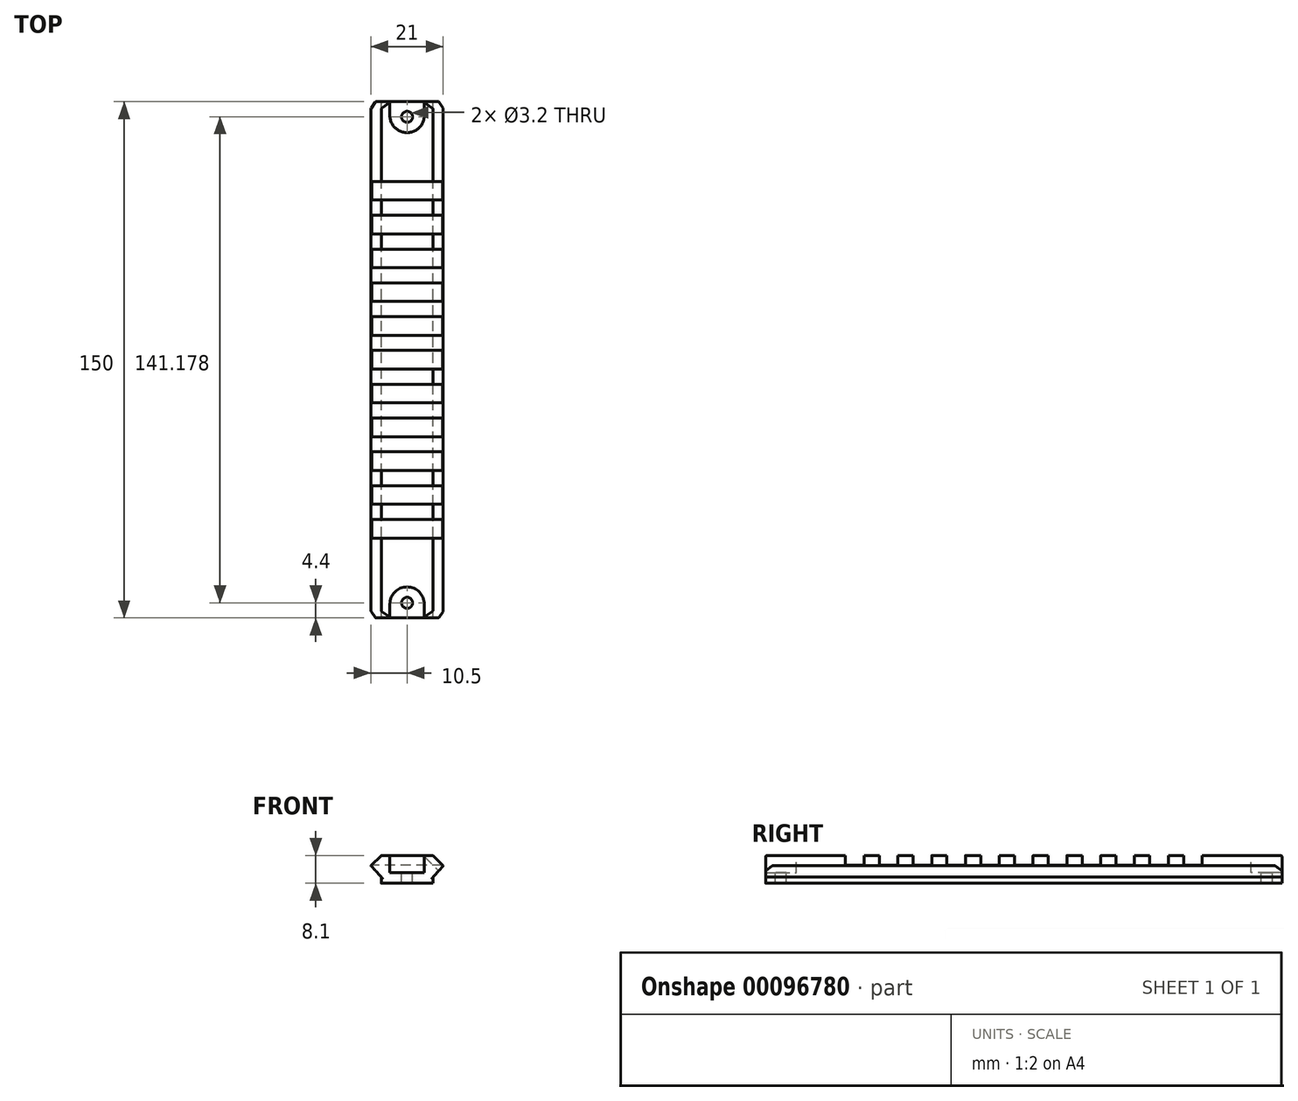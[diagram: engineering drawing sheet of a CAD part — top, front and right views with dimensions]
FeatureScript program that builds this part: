
annotation { "Feature Type Name" : "Feature", "Feature Type Description" : "" }
export const myFeature = defineFeature(function(context is Context, id is Id, definition is map)
    precondition{}
    {
        {
            var Q0;
            Q0=qCreatedBy(makeId("Front.planeOp"),FACE);
            var sketch = newSketch(context, id + "F0", { "sketchPlane" : qUnion([Q0])});
            skPoint(sketch, "E0", {"position": v(7.5, 0) * mm});
            skPoint(sketch, "E1", {"position": v(-7.5, 0) * mm});
            skPoint(sketch, "E2", {"position": v(0, 3.3) * mm});
            skPoint(sketch, "E3", {"position": v(0, -4.8) * mm});
            skLineSegment(sketch, "E4", {"start": v(7.5, -4.8) * mm, "end": v(-7.5, -4.8) * mm});
            skLineSegment(sketch, "E5", {"start": v(7.5, -4.8) * mm, "end": v(7.5, -3) * mm});
            skLineSegment(sketch, "E6", {"start": v(-7.5, -3) * mm, "end": v(-7.5, -4.8) * mm});
            skLineSegment(sketch, "E7", {"start": v(-7.5, -3) * mm, "end": v(-10.5, 0.3) * mm});
            skLineSegment(sketch, "E8", {"start": v(7.5, -3) * mm, "end": v(10.5, 0.3) * mm});
            skPoint(sketch, "E9", {"position": v(7.5, 3.3) * mm});
            skPoint(sketch, "E10", {"position": v(-7.5, 3.3) * mm});
            skLineSegment(sketch, "E11", {"start": v(-10.5, 0.3) * mm, "end": v(-7.5, 3.3) * mm});
            skLineSegment(sketch, "E12", {"start": v(10.5, 0.3) * mm, "end": v(7.5, 3.3) * mm});
            skLineSegment(sketch, "E13", {"start": v(-7.5, 3.3) * mm, "end": v(7.5, 3.3) * mm});
            skSolve(sketch);
        }
        {
            var Q0;
            Q0=qSketchRegion(id+"F0",true);
            extrude(context, id + "F1", {"entities" : qUnion([Q0]), "endBound" : BoundingType.SYMMETRIC, "depth" : 150 * mm});
        }
        {
            var Q0;
            Q0=makeQuery(id+"F1.opExtrude","SWEPT_FACE",FACE,{"disambiguationData":[OSD([sQuery(id+"F0.wireOp",EDGE,"E13")])]});
            var sketch = newSketch(context, id + "F2", { "sketchPlane" : qUnion([Q0])});
            skPoint(sketch, "E14", {"position": v(0, 2.7) * mm});
            skPoint(sketch, "E15", {"position": v(0, -2.7) * mm});
            skLineSegment(sketch, "E16", {"start": v(-14, -2.7) * mm, "end": v(14, -2.7) * mm});
            skLineSegment(sketch, "E17", {"start": v(14, -2.7) * mm, "end": v(14, 2.7) * mm});
            skLineSegment(sketch, "E18", {"start": v(14, 2.7) * mm, "end": v(-14, 2.7) * mm});
            skLineSegment(sketch, "E19", {"start": v(-14, -2.7) * mm, "end": v(-14, 2.7) * mm});
            skLineSegment(sketch, "E20", {"start": v(0, 75) * mm, "end": v(0, 60) * mm});
            skPoint(sketch, "E20.endSnap0", {"position": v(0, 75) * mm});
            skLineSegment(sketch, "E21.0.1.0", {"start": v(-14, 7.12) * mm, "end": v(-14, 12.52) * mm});
            skLineSegment(sketch, "E21.0.1.1", {"start": v(14.12, 12.52) * mm, "end": v(-14, 12.52) * mm});
            skLineSegment(sketch, "E21.0.1.2", {"start": v(-14, 7.12) * mm, "end": v(14.12, 7.12) * mm});
            skLineSegment(sketch, "E21.0.1.3", {"start": v(14.12, 7.12) * mm, "end": v(14.12, 12.52) * mm});
            skLineSegment(sketch, "E21.0.2.0", {"start": v(-14, 16.94) * mm, "end": v(-14, 22.34) * mm});
            skLineSegment(sketch, "E21.0.2.1", {"start": v(14.33, 22.34) * mm, "end": v(-14, 22.34) * mm});
            skLineSegment(sketch, "E21.0.2.2", {"start": v(-14, 16.94) * mm, "end": v(14.33, 16.94) * mm});
            skLineSegment(sketch, "E21.0.2.3", {"start": v(14.33, 16.94) * mm, "end": v(14.33, 22.34) * mm});
            skLineSegment(sketch, "E21.0.3.0", {"start": v(-14, 26.76) * mm, "end": v(-14, 32.16) * mm});
            skLineSegment(sketch, "E21.0.3.1", {"start": v(14.82, 32.16) * mm, "end": v(-14, 32.16) * mm});
            skLineSegment(sketch, "E21.0.3.2", {"start": v(-14, 26.76) * mm, "end": v(14.82, 26.76) * mm});
            skLineSegment(sketch, "E21.0.3.3", {"start": v(14.82, 26.76) * mm, "end": v(14.82, 32.16) * mm});
            skLineSegment(sketch, "E21.direction2", {"start": v(-14, -2.7) * mm, "end": v(-14, 7.12) * mm, "construction": true});
            skLineSegment(sketch, "E22.0.1.0", {"start": v(-14, -12.52) * mm, "end": v(14.53, -12.52) * mm});
            skLineSegment(sketch, "E22.0.1.1", {"start": v(-14, -12.52) * mm, "end": v(-14, -7.1) * mm});
            skLineSegment(sketch, "E22.0.1.2", {"start": v(14.53, -7.1) * mm, "end": v(-14, -7.1) * mm});
            skLineSegment(sketch, "E22.0.1.3", {"start": v(14.53, -12.52) * mm, "end": v(14.53, -7.1) * mm});
            skLineSegment(sketch, "E22.0.2.0", {"start": v(-14, -22.33) * mm, "end": v(15.6, -22.33) * mm});
            skLineSegment(sketch, "E22.0.2.1", {"start": v(-14, -22.33) * mm, "end": v(-14, -16.93) * mm});
            skLineSegment(sketch, "E22.0.2.2", {"start": v(15.6, -16.93) * mm, "end": v(-14, -16.93) * mm});
            skLineSegment(sketch, "E22.0.2.3", {"start": v(15.6, -22.33) * mm, "end": v(15.6, -16.93) * mm});
            skLineSegment(sketch, "E22.0.3.0", {"start": v(-14, -32.15) * mm, "end": v(15.9, -32.15) * mm});
            skLineSegment(sketch, "E22.0.3.1", {"start": v(-14, -32.15) * mm, "end": v(-14, -26.75) * mm});
            skLineSegment(sketch, "E22.0.3.2", {"start": v(15.9, -26.75) * mm, "end": v(-14, -26.75) * mm});
            skLineSegment(sketch, "E22.0.3.3", {"start": v(15.9, -32.15) * mm, "end": v(15.9, -26.75) * mm});
            skLineSegment(sketch, "E22.direction2", {"start": v(-14, -2.7) * mm, "end": v(-14, -12.52) * mm, "construction": true});
            skLineSegment(sketch, "E23.1.0.0", {"start": v(14.82, 41.98) * mm, "end": v(-14, 41.98) * mm});
            skLineSegment(sketch, "E23.1.0.1", {"start": v(-14, 36.58) * mm, "end": v(-14, 41.98) * mm});
            skLineSegment(sketch, "E23.1.0.2", {"start": v(-14, 36.58) * mm, "end": v(14.82, 36.58) * mm});
            skLineSegment(sketch, "E23.1.0.3", {"start": v(14.82, 36.58) * mm, "end": v(14.82, 41.98) * mm});
            skLineSegment(sketch, "E23.2.0.0", {"start": v(14.82, 51.8) * mm, "end": v(-14, 51.8) * mm});
            skLineSegment(sketch, "E23.2.0.1", {"start": v(-14, 46.4) * mm, "end": v(-14, 51.8) * mm});
            skLineSegment(sketch, "E23.2.0.2", {"start": v(-14, 46.4) * mm, "end": v(14.82, 46.4) * mm});
            skLineSegment(sketch, "E23.2.0.3", {"start": v(14.82, 46.4) * mm, "end": v(14.82, 51.8) * mm});
            skLineSegment(sketch, "E23.direction1", {"start": v(-14, 32.16) * mm, "end": v(-14, 41.98) * mm, "construction": true});
            skLineSegment(sketch, "E24.1.0.0", {"start": v(-14, -41.97) * mm, "end": v(15.9, -41.97) * mm});
            skLineSegment(sketch, "E24.1.0.1", {"start": v(-14, -41.97) * mm, "end": v(-14, -36.57) * mm});
            skLineSegment(sketch, "E24.1.0.2", {"start": v(15.9, -36.57) * mm, "end": v(-14, -36.57) * mm});
            skLineSegment(sketch, "E24.1.0.3", {"start": v(15.9, -41.97) * mm, "end": v(15.9, -36.57) * mm});
            skLineSegment(sketch, "E24.2.0.0", {"start": v(-14, -51.79) * mm, "end": v(15.9, -51.79) * mm});
            skLineSegment(sketch, "E24.2.0.1", {"start": v(-14, -51.79) * mm, "end": v(-14, -46.39) * mm});
            skLineSegment(sketch, "E24.2.0.2", {"start": v(15.9, -46.39) * mm, "end": v(-14, -46.39) * mm});
            skLineSegment(sketch, "E24.2.0.3", {"start": v(15.9, -51.79) * mm, "end": v(15.9, -46.39) * mm});
            skLineSegment(sketch, "E24.direction1", {"start": v(-14, -32.15) * mm, "end": v(-14, -41.97) * mm, "construction": true});
            skSolve(sketch);
        }
        {
            var Q0;
            Q0=qSketchRegion(id+"F2",true);
            extrude(context, id + "F3", {"entities" : qUnion([Q0]), "operationType" : NewBodyOperationType.REMOVE, "oppositeDirection" : true, "depth" : 2.8 * mm});
        }
        {
            var Q0;
            {var subQ0=sQuery(id+"F0.wireOp",EDGE,"E13");Q0=makeQuery(id+"F3.boolean.opBoolean","SPLIT",FACE,{"disambiguationData":[TD([makeQuery(id+"F3.opExtrude","SWEPT_FACE",FACE,{"disambiguationData":[OSD([sQuery(id+"F2.wireOp",EDGE,"E22.0.3.0")])]})])],"derivedFrom":makeQuery(id+"F1.opExtrude","SWEPT_FACE",FACE,{"disambiguationData":[OSD([subQ0])]})});}
            var sketch = newSketch(context, id + "F4", { "sketchPlane" : qUnion([Q0])});
            skLineSegment(sketch, "E25", {"start": v(-5, -73) * mm, "end": v(-5, -75) * mm});
            skLineSegment(sketch, "E26", {"start": v(-5, -73) * mm, "end": v(-5, -71) * mm});
            skLineSegment(sketch, "E27", {"start": v(5, -75) * mm, "end": v(5, -73) * mm});
            skLineSegment(sketch, "E28", {"start": v(5, -73) * mm, "end": v(5, -71) * mm});
            skArc(sketch, "E29", {"start": v(5, -71) * mm, "mid": v(0, -66) * mm, "end": v(-5, -71) * mm});
            skArc(sketch, "E30.MirrorCS", {"start": v(5, 71) * mm, "mid": v(0, 65.98) * mm, "end": v(-5, 71) * mm});
            skLineSegment(sketch, "E31.MirrorCS", {"start": v(-5, 73) * mm, "end": v(-5, 71) * mm});
            skLineSegment(sketch, "E32.MirrorCS", {"start": v(5, 73) * mm, "end": v(5, 71) * mm});
            skLineSegment(sketch, "E33.MirrorCS", {"start": v(5, 75) * mm, "end": v(5, 73) * mm});
            skLineSegment(sketch, "E34.MirrorCS", {"start": v(-5, 73) * mm, "end": v(-5, 75) * mm});
            skLineSegment(sketch, "E35", {"start": v(-5, -75) * mm, "end": v(5, -75) * mm});
            skLineSegment(sketch, "E36", {"start": v(-5, 75) * mm, "end": v(5, 75) * mm});
            skSolve(sketch);
        }
        {
            var Q0;
            Q0=qSketchRegion(id+"F4",true);
            extrude(context, id + "F5", {"entities" : qUnion([Q0]), "operationType" : NewBodyOperationType.REMOVE, "oppositeDirection" : true, "depth" : 5 * mm});
        }
        {
            var Q0;
            Q0=makeQuery(id+"F5.boolean.opBoolean","COPY",FACE,{"derivedFrom":makeQuery(id+"F5.opExtrude","CAP_FACE",FACE,{"disambiguationData":[OSD([sQuery(id+"F4.wireOp",EDGE,"E25"),sQuery(id+"F4.wireOp",EDGE,"E26"),sQuery(id+"F4.wireOp",EDGE,"E27"),sQuery(id+"F4.wireOp",EDGE,"E28"),sQuery(id+"F4.wireOp",EDGE,"E29"),sQuery(id+"F4.wireOp",EDGE,"E35")])],"isStart":false})});
            var sketch = newSketch(context, id + "F6", { "sketchPlane" : qUnion([Q0])});
            skCircle(sketch, "E37", {"center": v(0, -70.6) * mm, "radius": 1.6 * mm});
            skCircle(sketch, "E38", {"center": v(0, 70.58) * mm, "radius": 1.6 * mm});
            skSolve(sketch);
        }
        {
            var Q0;
            Q0=qSketchRegion(id+"F6",true);
            extrude(context, id + "F7", {"entities" : qUnion([Q0]), "operationType" : NewBodyOperationType.REMOVE, "endBound" : BoundingType.THROUGH_ALL, "oppositeDirection" : true, "depth" : 25 * mm});
        }
        {
            var Q0;
            Q0=makeQuery(id+"F1.opExtrude","CAP_EDGE",EDGE,{"disambiguationData":[OSD([sQuery(id+"F0.wireOp",EDGE,"E12")])],"isStart":true});
            var Q1;
            Q1=makeQuery(id+"F1.opExtrude","CAP_EDGE",EDGE,{"disambiguationData":[OSD([sQuery(id+"F0.wireOp",EDGE,"E11")])],"isStart":true});
            var Q2;
            Q2=makeQuery(id+"F1.opExtrude","CAP_EDGE",EDGE,{"disambiguationData":[OSD([sQuery(id+"F0.wireOp",EDGE,"E12")])],"isStart":false});
            var Q3;
            Q3=makeQuery(id+"F1.opExtrude","CAP_EDGE",EDGE,{"disambiguationData":[OSD([sQuery(id+"F0.wireOp",EDGE,"E11")])],"isStart":false});
            chamfer(context, id + "F8", {"entities" : qUnion([Q0, Q1, Q2, Q3]), "width" : 2 * mm, "tangentPropagation" : true});
        }
        {
            var Q0;
            {var subQ0=sQuery(id+"F0.wireOp",EDGE,"E11");var subQ1=sQuery(id+"F0.wireOp",EDGE,"E13");Q0=makeQuery(id+"F3.boolean.opBoolean","SPLIT",EDGE,{"disambiguationData":[TD([makeQuery(id+"F3.opExtrude","SWEPT_FACE",FACE,{"disambiguationData":[OSD([sQuery(id+"F2.wireOp",EDGE,"E21.0.2.1")])]})])],"derivedFrom":makeQuery(id+"F1.opExtrude","SWEPT_EDGE",EDGE,{"disambiguationData":[OSD([subQ0,subQ1])]})});}
            var Q1;
            {var subQ0=sQuery(id+"F0.wireOp",EDGE,"E11");var subQ1=sQuery(id+"F0.wireOp",EDGE,"E13");Q1=makeQuery(id+"F3.boolean.opBoolean","SPLIT",EDGE,{"disambiguationData":[TD([makeQuery(id+"F3.opExtrude","SWEPT_FACE",FACE,{"disambiguationData":[OSD([sQuery(id+"F2.wireOp",EDGE,"E21.0.1.1")])]})])],"derivedFrom":makeQuery(id+"F1.opExtrude","SWEPT_EDGE",EDGE,{"disambiguationData":[OSD([subQ0,subQ1])]})});}
            var Q2;
            {var subQ0=sQuery(id+"F0.wireOp",EDGE,"E11");var subQ1=sQuery(id+"F0.wireOp",EDGE,"E13");Q2=makeQuery(id+"F3.boolean.opBoolean","SPLIT",EDGE,{"disambiguationData":[TD([makeQuery(id+"F3.opExtrude","SWEPT_FACE",FACE,{"disambiguationData":[OSD([sQuery(id+"F2.wireOp",EDGE,"E18")])]})])],"derivedFrom":makeQuery(id+"F1.opExtrude","SWEPT_EDGE",EDGE,{"disambiguationData":[OSD([subQ0,subQ1])]})});}
            var Q3;
            {var subQ0=sQuery(id+"F0.wireOp",EDGE,"E11");var subQ1=sQuery(id+"F0.wireOp",EDGE,"E13");Q3=makeQuery(id+"F3.boolean.opBoolean","SPLIT",EDGE,{"disambiguationData":[TD([makeQuery(id+"F3.opExtrude","SWEPT_FACE",FACE,{"disambiguationData":[OSD([sQuery(id+"F2.wireOp",EDGE,"E16")])]})])],"derivedFrom":makeQuery(id+"F1.opExtrude","SWEPT_EDGE",EDGE,{"disambiguationData":[OSD([subQ0,subQ1])]})});}
            var Q4;
            {var subQ0=sQuery(id+"F0.wireOp",EDGE,"E11");var subQ1=sQuery(id+"F0.wireOp",EDGE,"E13");Q4=makeQuery(id+"F3.boolean.opBoolean","SPLIT",EDGE,{"disambiguationData":[TD([makeQuery(id+"F3.opExtrude","SWEPT_FACE",FACE,{"disambiguationData":[OSD([sQuery(id+"F2.wireOp",EDGE,"E22.0.1.0")])]})])],"derivedFrom":makeQuery(id+"F1.opExtrude","SWEPT_EDGE",EDGE,{"disambiguationData":[OSD([subQ0,subQ1])]})});}
            var Q5;
            {var subQ0=sQuery(id+"F0.wireOp",EDGE,"E11");var subQ1=sQuery(id+"F0.wireOp",EDGE,"E13");Q5=makeQuery(id+"F3.boolean.opBoolean","SPLIT",EDGE,{"disambiguationData":[TD([makeQuery(id+"F3.opExtrude","SWEPT_FACE",FACE,{"disambiguationData":[OSD([sQuery(id+"F2.wireOp",EDGE,"E22.0.2.0")])]})])],"derivedFrom":makeQuery(id+"F1.opExtrude","SWEPT_EDGE",EDGE,{"disambiguationData":[OSD([subQ0,subQ1])]})});}
            var Q6;
            {var subQ0=sQuery(id+"F0.wireOp",EDGE,"E12");var subQ1=sQuery(id+"F0.wireOp",EDGE,"E13");Q6=makeQuery(id+"F3.boolean.opBoolean","SPLIT",EDGE,{"disambiguationData":[TD([makeQuery(id+"F3.opExtrude","SWEPT_FACE",FACE,{"disambiguationData":[OSD([sQuery(id+"F2.wireOp",EDGE,"E22.0.2.0")])]})])],"derivedFrom":makeQuery(id+"F1.opExtrude","SWEPT_EDGE",EDGE,{"disambiguationData":[OSD([subQ0,subQ1])]})});}
            var Q7;
            {var subQ0=sQuery(id+"F0.wireOp",EDGE,"E12");var subQ1=sQuery(id+"F0.wireOp",EDGE,"E13");Q7=makeQuery(id+"F3.boolean.opBoolean","SPLIT",EDGE,{"disambiguationData":[TD([makeQuery(id+"F3.opExtrude","SWEPT_FACE",FACE,{"disambiguationData":[OSD([sQuery(id+"F2.wireOp",EDGE,"E22.0.1.0")])]})])],"derivedFrom":makeQuery(id+"F1.opExtrude","SWEPT_EDGE",EDGE,{"disambiguationData":[OSD([subQ0,subQ1])]})});}
            var Q8;
            {var subQ0=sQuery(id+"F0.wireOp",EDGE,"E12");var subQ1=sQuery(id+"F0.wireOp",EDGE,"E13");Q8=makeQuery(id+"F3.boolean.opBoolean","SPLIT",EDGE,{"disambiguationData":[TD([makeQuery(id+"F3.opExtrude","SWEPT_FACE",FACE,{"disambiguationData":[OSD([sQuery(id+"F2.wireOp",EDGE,"E18")])]})])],"derivedFrom":makeQuery(id+"F1.opExtrude","SWEPT_EDGE",EDGE,{"disambiguationData":[OSD([subQ0,subQ1])]})});}
            var Q9;
            {var subQ0=sQuery(id+"F0.wireOp",EDGE,"E12");var subQ1=sQuery(id+"F0.wireOp",EDGE,"E13");Q9=makeQuery(id+"F3.boolean.opBoolean","SPLIT",EDGE,{"disambiguationData":[TD([makeQuery(id+"F3.opExtrude","SWEPT_FACE",FACE,{"disambiguationData":[OSD([sQuery(id+"F2.wireOp",EDGE,"E21.0.1.1")])]})])],"derivedFrom":makeQuery(id+"F1.opExtrude","SWEPT_EDGE",EDGE,{"disambiguationData":[OSD([subQ0,subQ1])]})});}
            var Q10;
            {var subQ0=sQuery(id+"F0.wireOp",EDGE,"E12");var subQ1=sQuery(id+"F0.wireOp",EDGE,"E13");Q10=makeQuery(id+"F3.boolean.opBoolean","SPLIT",EDGE,{"disambiguationData":[TD([makeQuery(id+"F3.opExtrude","SWEPT_FACE",FACE,{"disambiguationData":[OSD([sQuery(id+"F2.wireOp",EDGE,"E21.0.2.1")])]})])],"derivedFrom":makeQuery(id+"F1.opExtrude","SWEPT_EDGE",EDGE,{"disambiguationData":[OSD([subQ0,subQ1])]})});}
            var Q11;
            {var subQ0=sQuery(id+"F0.wireOp",EDGE,"E13");var subQ2=sQuery(id+"F0.wireOp",EDGE,"E11");Q11=makeQuery(id+"F8.opChamfer","BLEND_EDGE",EDGE,{"blendedFrom":[makeQuery(id+"F1.opExtrude","CAP_EDGE",EDGE,{"disambiguationData":[OSD([subQ2])],"isStart":true}),makeQuery(id+"F3.boolean.opBoolean","SPLIT",FACE,{"disambiguationData":[TD([makeQuery(id+"F3.opExtrude","SWEPT_FACE",FACE,{"disambiguationData":[OSD([sQuery(id+"F2.wireOp",EDGE,"E21.0.3.1")])]})])],"derivedFrom":makeQuery(id+"F1.opExtrude","SWEPT_FACE",FACE,{"disambiguationData":[OSD([subQ0])]})})],"blendedInto":[makeQuery(id+"F3.boolean.opBoolean","SPLIT",FACE,{"disambiguationData":[TD([makeQuery(id+"F3.opExtrude","SWEPT_FACE",FACE,{"disambiguationData":[OSD([sQuery(id+"F2.wireOp",EDGE,"E21.0.3.1")])]})])],"derivedFrom":makeQuery(id+"F1.opExtrude","SWEPT_FACE",FACE,{"disambiguationData":[OSD([subQ0])]})})]});}
            var Q12;
            {var subQ0=sQuery(id+"F0.wireOp",EDGE,"E11");Q12=makeQuery(id+"F8.opChamfer","BLEND_EDGE",EDGE,{"blendedFrom":[makeQuery(id+"F1.opExtrude","CAP_EDGE",EDGE,{"disambiguationData":[OSD([subQ0])],"isStart":true}),makeQuery(id+"F1.opExtrude","CAP_FACE",FACE,{"disambiguationData":[OSD([sQuery(id+"F0.wireOp",EDGE,"E4"),sQuery(id+"F0.wireOp",EDGE,"E5"),sQuery(id+"F0.wireOp",EDGE,"E6"),sQuery(id+"F0.wireOp",EDGE,"E7"),sQuery(id+"F0.wireOp",EDGE,"E8"),subQ0,sQuery(id+"F0.wireOp",EDGE,"E12"),sQuery(id+"F0.wireOp",EDGE,"E13")])],"isStart":true})],"blendedInto":[makeQuery(id+"F1.opExtrude","CAP_FACE",FACE,{"disambiguationData":[OSD([sQuery(id+"F0.wireOp",EDGE,"E4"),sQuery(id+"F0.wireOp",EDGE,"E5"),sQuery(id+"F0.wireOp",EDGE,"E6"),sQuery(id+"F0.wireOp",EDGE,"E7"),sQuery(id+"F0.wireOp",EDGE,"E8"),subQ0,sQuery(id+"F0.wireOp",EDGE,"E12"),sQuery(id+"F0.wireOp",EDGE,"E13")])],"isStart":true})]});}
            var Q13;
            {var subQ0=sQuery(id+"F0.wireOp",EDGE,"E13");var subQ1=sQuery(id+"F0.wireOp",EDGE,"E12");Q13=makeQuery(id+"F8.opChamfer","BLEND_EDGE",EDGE,{"blendedFrom":[makeQuery(id+"F1.opExtrude","CAP_EDGE",EDGE,{"disambiguationData":[OSD([subQ1])],"isStart":true}),makeQuery(id+"F3.boolean.opBoolean","SPLIT",FACE,{"disambiguationData":[TD([makeQuery(id+"F3.opExtrude","SWEPT_FACE",FACE,{"disambiguationData":[OSD([sQuery(id+"F2.wireOp",EDGE,"E21.0.3.1")])]})])],"derivedFrom":makeQuery(id+"F1.opExtrude","SWEPT_FACE",FACE,{"disambiguationData":[OSD([subQ0])]})})],"blendedInto":[makeQuery(id+"F3.boolean.opBoolean","SPLIT",FACE,{"disambiguationData":[TD([makeQuery(id+"F3.opExtrude","SWEPT_FACE",FACE,{"disambiguationData":[OSD([sQuery(id+"F2.wireOp",EDGE,"E21.0.3.1")])]})])],"derivedFrom":makeQuery(id+"F1.opExtrude","SWEPT_FACE",FACE,{"disambiguationData":[OSD([subQ0])]})})]});}
            var Q14;
            {var subQ0=sQuery(id+"F0.wireOp",EDGE,"E12");Q14=makeQuery(id+"F8.opChamfer","BLEND_EDGE",EDGE,{"blendedFrom":[makeQuery(id+"F1.opExtrude","CAP_EDGE",EDGE,{"disambiguationData":[OSD([subQ0])],"isStart":true}),makeQuery(id+"F1.opExtrude","SWEPT_FACE",FACE,{"disambiguationData":[OSD([subQ0])]})],"blendedInto":[makeQuery(id+"F1.opExtrude","SWEPT_FACE",FACE,{"disambiguationData":[OSD([subQ0])]})]});}
            var Q15;
            {var subQ0=sQuery(id+"F0.wireOp",EDGE,"E11");Q15=makeQuery(id+"F8.opChamfer","BLEND_EDGE",EDGE,{"blendedFrom":[makeQuery(id+"F1.opExtrude","CAP_EDGE",EDGE,{"disambiguationData":[OSD([subQ0])],"isStart":true}),makeQuery(id+"F1.opExtrude","SWEPT_FACE",FACE,{"disambiguationData":[OSD([subQ0])]})],"blendedInto":[makeQuery(id+"F1.opExtrude","SWEPT_FACE",FACE,{"disambiguationData":[OSD([subQ0])]})]});}
            var Q16;
            {var subQ0=sQuery(id+"F0.wireOp",EDGE,"E12");Q16=makeQuery(id+"F8.opChamfer","BLEND_EDGE",EDGE,{"blendedFrom":[makeQuery(id+"F1.opExtrude","CAP_EDGE",EDGE,{"disambiguationData":[OSD([subQ0])],"isStart":false}),makeQuery(id+"F1.opExtrude","CAP_FACE",FACE,{"disambiguationData":[OSD([sQuery(id+"F0.wireOp",EDGE,"E4"),sQuery(id+"F0.wireOp",EDGE,"E5"),sQuery(id+"F0.wireOp",EDGE,"E6"),sQuery(id+"F0.wireOp",EDGE,"E7"),sQuery(id+"F0.wireOp",EDGE,"E8"),sQuery(id+"F0.wireOp",EDGE,"E11"),subQ0,sQuery(id+"F0.wireOp",EDGE,"E13")])],"isStart":false})],"blendedInto":[makeQuery(id+"F1.opExtrude","CAP_FACE",FACE,{"disambiguationData":[OSD([sQuery(id+"F0.wireOp",EDGE,"E4"),sQuery(id+"F0.wireOp",EDGE,"E5"),sQuery(id+"F0.wireOp",EDGE,"E6"),sQuery(id+"F0.wireOp",EDGE,"E7"),sQuery(id+"F0.wireOp",EDGE,"E8"),sQuery(id+"F0.wireOp",EDGE,"E11"),subQ0,sQuery(id+"F0.wireOp",EDGE,"E13")])],"isStart":false})]});}
            var Q17;
            {var subQ0=sQuery(id+"F0.wireOp",EDGE,"E12");Q17=makeQuery(id+"F8.opChamfer","BLEND_EDGE",EDGE,{"blendedFrom":[makeQuery(id+"F1.opExtrude","CAP_EDGE",EDGE,{"disambiguationData":[OSD([subQ0])],"isStart":false}),makeQuery(id+"F1.opExtrude","SWEPT_FACE",FACE,{"disambiguationData":[OSD([subQ0])]})],"blendedInto":[makeQuery(id+"F1.opExtrude","SWEPT_FACE",FACE,{"disambiguationData":[OSD([subQ0])]})]});}
            var Q18;
            {var subQ0=sQuery(id+"F0.wireOp",EDGE,"E13");var subQ1=sQuery(id+"F0.wireOp",EDGE,"E12");Q18=makeQuery(id+"F8.opChamfer","BLEND_EDGE",EDGE,{"blendedFrom":[makeQuery(id+"F1.opExtrude","CAP_EDGE",EDGE,{"disambiguationData":[OSD([subQ1])],"isStart":false}),makeQuery(id+"F3.boolean.opBoolean","SPLIT",FACE,{"disambiguationData":[TD([makeQuery(id+"F3.opExtrude","SWEPT_FACE",FACE,{"disambiguationData":[OSD([sQuery(id+"F2.wireOp",EDGE,"E22.0.3.0")])]})])],"derivedFrom":makeQuery(id+"F1.opExtrude","SWEPT_FACE",FACE,{"disambiguationData":[OSD([subQ0])]})})],"blendedInto":[makeQuery(id+"F3.boolean.opBoolean","SPLIT",FACE,{"disambiguationData":[TD([makeQuery(id+"F3.opExtrude","SWEPT_FACE",FACE,{"disambiguationData":[OSD([sQuery(id+"F2.wireOp",EDGE,"E22.0.3.0")])]})])],"derivedFrom":makeQuery(id+"F1.opExtrude","SWEPT_FACE",FACE,{"disambiguationData":[OSD([subQ0])]})})]});}
            var Q19;
            {var subQ0=sQuery(id+"F0.wireOp",EDGE,"E11");Q19=makeQuery(id+"F8.opChamfer","BLEND_EDGE",EDGE,{"blendedFrom":[makeQuery(id+"F1.opExtrude","CAP_EDGE",EDGE,{"disambiguationData":[OSD([subQ0])],"isStart":false}),makeQuery(id+"F1.opExtrude","CAP_FACE",FACE,{"disambiguationData":[OSD([sQuery(id+"F0.wireOp",EDGE,"E4"),sQuery(id+"F0.wireOp",EDGE,"E5"),sQuery(id+"F0.wireOp",EDGE,"E6"),sQuery(id+"F0.wireOp",EDGE,"E7"),sQuery(id+"F0.wireOp",EDGE,"E8"),subQ0,sQuery(id+"F0.wireOp",EDGE,"E12"),sQuery(id+"F0.wireOp",EDGE,"E13")])],"isStart":false})],"blendedInto":[makeQuery(id+"F1.opExtrude","CAP_FACE",FACE,{"disambiguationData":[OSD([sQuery(id+"F0.wireOp",EDGE,"E4"),sQuery(id+"F0.wireOp",EDGE,"E5"),sQuery(id+"F0.wireOp",EDGE,"E6"),sQuery(id+"F0.wireOp",EDGE,"E7"),sQuery(id+"F0.wireOp",EDGE,"E8"),subQ0,sQuery(id+"F0.wireOp",EDGE,"E12"),sQuery(id+"F0.wireOp",EDGE,"E13")])],"isStart":false})]});}
            var Q20;
            {var subQ0=sQuery(id+"F0.wireOp",EDGE,"E13");var subQ2=sQuery(id+"F0.wireOp",EDGE,"E11");Q20=makeQuery(id+"F8.opChamfer","BLEND_EDGE",EDGE,{"blendedFrom":[makeQuery(id+"F1.opExtrude","CAP_EDGE",EDGE,{"disambiguationData":[OSD([subQ2])],"isStart":false}),makeQuery(id+"F3.boolean.opBoolean","SPLIT",FACE,{"disambiguationData":[TD([makeQuery(id+"F3.opExtrude","SWEPT_FACE",FACE,{"disambiguationData":[OSD([sQuery(id+"F2.wireOp",EDGE,"E22.0.3.0")])]})])],"derivedFrom":makeQuery(id+"F1.opExtrude","SWEPT_FACE",FACE,{"disambiguationData":[OSD([subQ0])]})})],"blendedInto":[makeQuery(id+"F3.boolean.opBoolean","SPLIT",FACE,{"disambiguationData":[TD([makeQuery(id+"F3.opExtrude","SWEPT_FACE",FACE,{"disambiguationData":[OSD([sQuery(id+"F2.wireOp",EDGE,"E22.0.3.0")])]})])],"derivedFrom":makeQuery(id+"F1.opExtrude","SWEPT_FACE",FACE,{"disambiguationData":[OSD([subQ0])]})})]});}
            var Q21;
            {var subQ0=sQuery(id+"F0.wireOp",EDGE,"E11");Q21=makeQuery(id+"F8.opChamfer","BLEND_EDGE",EDGE,{"blendedFrom":[makeQuery(id+"F1.opExtrude","CAP_EDGE",EDGE,{"disambiguationData":[OSD([subQ0])],"isStart":false}),makeQuery(id+"F1.opExtrude","SWEPT_FACE",FACE,{"disambiguationData":[OSD([subQ0])]})],"blendedInto":[makeQuery(id+"F1.opExtrude","SWEPT_FACE",FACE,{"disambiguationData":[OSD([subQ0])]})]});}
            var Q22;
            Q22=makeQuery(id+"F1.opExtrude","CAP_EDGE",EDGE,{"disambiguationData":[OSD([sQuery(id+"F0.wireOp",EDGE,"E6")])],"isStart":false});
            var Q23;
            Q23=makeQuery(id+"F1.opExtrude","CAP_EDGE",EDGE,{"disambiguationData":[OSD([sQuery(id+"F0.wireOp",EDGE,"E5")])],"isStart":false});
            var Q24;
            Q24=makeQuery(id+"F1.opExtrude","CAP_EDGE",EDGE,{"disambiguationData":[OSD([sQuery(id+"F0.wireOp",EDGE,"E5")])],"isStart":true});
            var Q25;
            Q25=makeQuery(id+"F1.opExtrude","CAP_EDGE",EDGE,{"disambiguationData":[OSD([sQuery(id+"F0.wireOp",EDGE,"E6")])],"isStart":true});
            fillet(context, id + "F9", {"entities" : qUnion([Q0, Q1, Q2, Q3, Q4, Q5, Q6, Q7, Q8, Q9, Q10, Q11, Q12, Q13, Q14, Q15, Q16, Q17, Q18, Q19, Q20, Q21, Q22, Q23, Q24, Q25]), "radius" : 0.5 * mm, "tangentPropagation" : true, "allowEdgeOverflow" : false});
        }
    });
